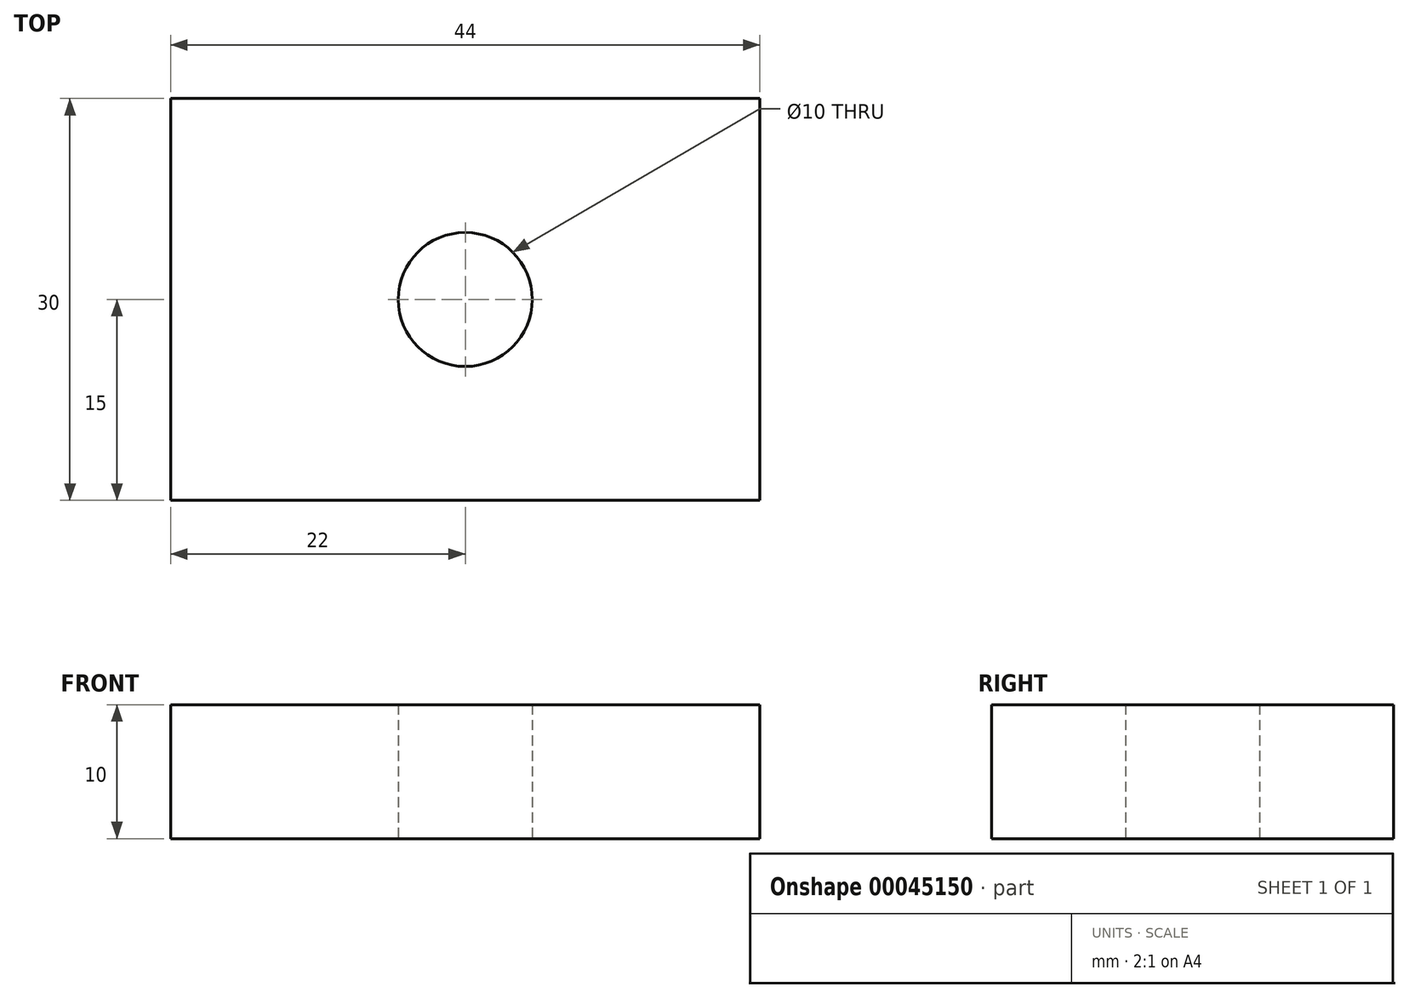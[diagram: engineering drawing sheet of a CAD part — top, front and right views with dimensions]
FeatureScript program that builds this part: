
annotation { "Feature Type Name" : "Feature", "Feature Type Description" : "" }
export const myFeature = defineFeature(function(context is Context, id is Id, definition is map)
    precondition{}
    {
        {
            var Q0;
            Q0=qCreatedBy(makeId("Top.planeOp"),FACE);
            var sketch = newSketch(context, id + "F0", { "sketchPlane" : qUnion([Q0])});
            skLineSegment(sketch, "E0", {"start": v(0, 0) * mm, "end": v(44, 0) * mm});
            skLineSegment(sketch, "E1", {"start": v(0, 0) * mm, "end": v(0, 30) * mm});
            skLineSegment(sketch, "E2", {"start": v(44, 0) * mm, "end": v(44, 30) * mm});
            skLineSegment(sketch, "E3", {"start": v(0, 30) * mm, "end": v(44, 30) * mm});
            skLineSegment(sketch, "E4", {"start": v(22, 30) * mm, "end": v(22, 0) * mm, "construction": true});
            skLineSegment(sketch, "E5", {"start": v(0, 15) * mm, "end": v(44, 15) * mm, "construction": true});
            skCircle(sketch, "E6", {"center": v(22, 15) * mm, "radius": 5 * mm});
            skLineSegment(sketch, "E7", {"start": v(18.8, 18.84) * mm, "end": v(22, 15) * mm, "construction": true});
            skSolve(sketch);
        }
        {
            var Q0;
            Q0=makeQuery(id+"F0.imprint","IMPRINT",FACE,{"disambiguationData":[TD([[makeQuery(id+"F0.imprint","IMPRINT",EDGE,{"derivedFrom":sQuery(id+"F0.wireOp",EDGE,"E0")}),1.0]])]});
            extrude(context, id + "F1", {"entities" : qUnion([Q0]), "depth" : 10 * mm});
        }
    });
